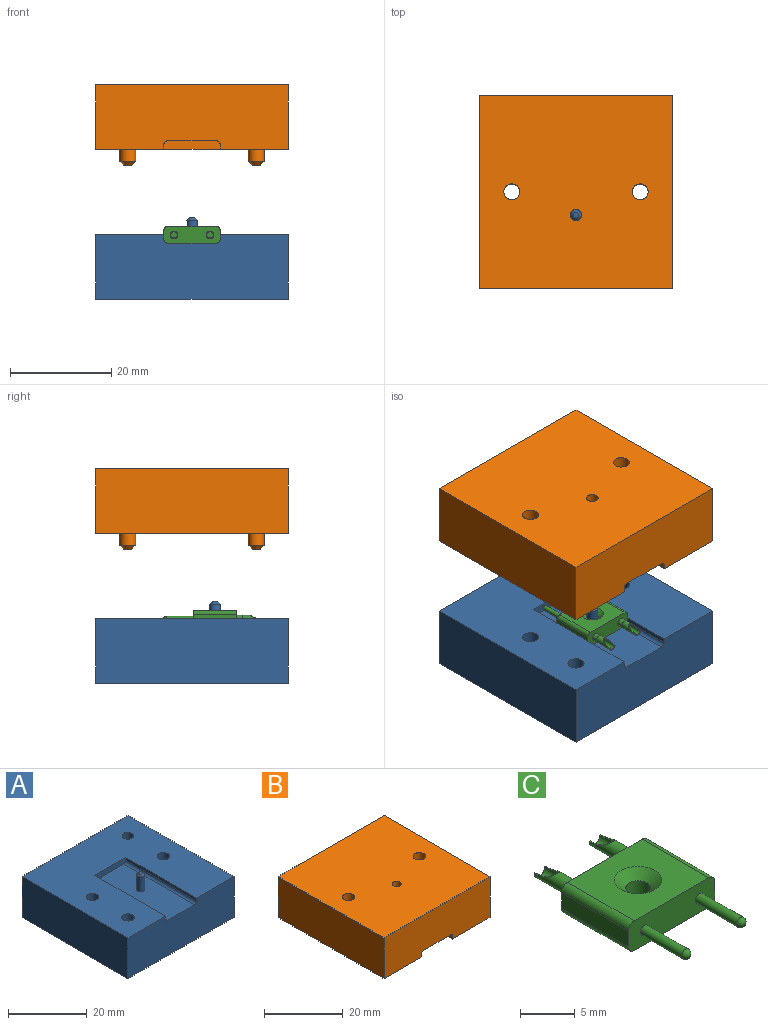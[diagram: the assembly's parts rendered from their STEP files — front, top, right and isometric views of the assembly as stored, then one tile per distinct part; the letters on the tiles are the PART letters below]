
ASSEMBLY  parts=3 mates=3
PART A: 21 faces, bbox 38.1x38.1x16.1 mm
  f0: plane 38.1x38.1mm, normal (0,0,1), area 1137.2mm2, adj f1,f2,f3,f4,f6,f7,f8,f13
  f1: plane 38.1x12.7mm, normal (-1,0,0), area 483.9mm2, adj f0,f2,f4,f5
  f2: plane 38.1x12.7mm, normal (0,-1,0), area 465.7mm2, adj f0,f1,f3,f5,f6,f7,f9,f19
  f3: plane 38.1x12.7mm, normal (1,0,0), area 483.9mm2, adj f0,f2,f4,f5
  f4: plane 38.1x12.7mm, normal (0,1,0), area 483.9mm2, adj f0,f1,f3,f5
  f5: plane 38.1x38.1mm, normal (0,0,-1), area 1435.8mm2, adj f1,f2,f3,f4,f13,f14
  f6: plane 25.4x0.89mm, normal (1,0,0), area 22.6mm2, adj f0,f2,f8,f20
  f7: plane 25.4x0.89mm, normal (-1,0,0), area 22.6mm2, adj f0,f2,f8,f19
  f8: plane 11.18x1.65mm, normal (0,-1,0), area 18.2mm2, adj f0,f6,f7,f9,f19,f20
  f9: plane 25.4x9.65mm, normal (0,0,1), area 241.5mm2, adj f2,f8,f10,f19,f20
  f10: cylinder r=1.08mm len=4.57mm, axis (0,0,-1), area 31mm2, adj f9,f12
  f11: plane 1.14x1.14mm, normal (0,0,1), area 1mm2, adj f12
  f12: cone r=0.57mm half-angle=45deg, axis (0,0,-1), area 3.7mm2, adj f10,f11
  f13: cylinder r=1.59mm len=12.7mm, axis (0,0,1), area 126.7mm2, adj f0,f5
  f14: cylinder r=1.59mm len=12.7mm, axis (0,0,1), area 126.7mm2, adj f0,f5
  f15: cylinder r=1.47mm len=6.35mm, axis (0,0,1), area 58.7mm2, adj f0,f16
  f16: plane 2.95x2.95mm, normal (0,0,1), area 6.8mm2, adj f15
  f17: cylinder r=1.59mm len=6.35mm, axis (0,0,1), area 63.3mm2, adj f0,f18
  f18: plane 3.18x3.18mm, normal (0,0,1), area 7.9mm2, adj f17
  f19: cylinder r=0.76mm len=25.4mm, axis (0,1,0), area 30.4mm2, adj f2,f7,f8,f9
  f20: cylinder r=0.76mm len=25.4mm, axis (0,-1,0), area 30.4mm2, adj f2,f6,f8,f9
PART B: 21 faces, bbox 38.1x38.1x15.9 mm
  f0: plane 38.1x38.1mm, normal (0,0,-1), area 1136.6mm2, adj f1,f2,f3,f4,f6,f7,f8,f13
  f1: plane 38.1x12.7mm, normal (-1,0,0), area 483.9mm2, adj f0,f2,f4,f5
  f2: plane 38.1x12.7mm, normal (0,-1,0), area 465.7mm2, adj f0,f1,f3,f5,f6,f8,f9,f11
  f3: plane 38.1x12.7mm, normal (1,0,0), area 483.9mm2, adj f0,f2,f4,f5
  f4: plane 38.1x12.7mm, normal (0,1,0), area 483.9mm2, adj f0,f1,f3,f5
  f5: plane 38.1x38.1mm, normal (0,0,1), area 1431.7mm2, adj f1,f2,f3,f4,f10,f13,f14
  f6: plane 25.4x0.89mm, normal (1,0,0), area 22.6mm2, adj f0,f2,f7,f11
  f7: plane 11.18x1.65mm, normal (0,-1,0), area 18.2mm2, adj f0,f6,f8,f9,f11,f12
  f8: plane 25.4x0.89mm, normal (-1,0,0), area 22.6mm2, adj f0,f2,f7,f12
  f9: plane 25.4x9.65mm, normal (0,0,-1), area 241.1mm2, adj f2,f7,f10,f11,f12
  f10: cylinder r=1.14mm len=11.05mm, axis (0,0,-1), area 79.4mm2, adj f5,f9
  f11: cylinder r=0.76mm len=25.4mm, axis (0,1,0), area 30.4mm2, adj f2,f6,f7,f9
  f12: cylinder r=0.76mm len=25.4mm, axis (0,-1,0), area 30.4mm2, adj f2,f7,f8,f9
  f13: cylinder r=1.59mm len=12.7mm, axis (0,0,-1), area 126.7mm2, adj f0,f5
  f14: cylinder r=1.59mm len=12.7mm, axis (0,0,-1), area 126.7mm2, adj f0,f5
  f15: cylinder r=1.56mm len=3.12mm, axis (0,0,1), area 23.7mm2, adj f0,f20
  f16: plane 1.6x1.6mm, normal (0,0,-1), area 2mm2, adj f20
  f17: cylinder r=1.56mm len=3.12mm, axis (0,0,1), area 23.7mm2, adj f0,f19
  f18: plane 1.6x1.6mm, normal (0,0,-1), area 2mm2, adj f19
  f19: cone r=0.8mm half-angle=45deg, axis (0,0,1), area 8mm2, adj f17,f18
  f20: cone r=0.8mm half-angle=45deg, axis (0,0,1), area 8mm2, adj f15,f16
PART C: 26 faces, bbox 11.2x19.3x3.3 mm
  f0: cylinder r=1.14mm len=2.42mm, axis (0,0,1), area 17.4mm2, adj f4,f21
  f1: plane 1.52x0.76mm, normal (0,1,0), area 0.3mm2, adj f13,f15,f20
  f2: plane 1.52x0.76mm, normal (0,1,0), area 0.3mm2, adj f14,f17,f19
  f3: plane 8.64x1.78mm, normal (-1,0,0), area 15.4mm2, adj f7,f8,f22,f25
  f4: plane 9.65x8.64mm, normal (0,0,-1), area 79.3mm2, adj f0,f7,f8,f22,f23
  f5: plane 8.64x1.78mm, normal (1,0,0), area 15.4mm2, adj f7,f8,f23,f24
  f6: plane 9.65x8.64mm, normal (0,0,1), area 68.7mm2, adj f7,f8,f21,f24,f25
  f7: plane 11.18x3.3mm, normal (0,1,0), area 32.8mm2, adj f3,f4,f5,f6,f13,f14,f22,f23
  f8: plane 11.18x3.3mm, normal (0,-1,0), area 34.8mm2, adj f3,f4,f5,f6,f9,f10,f22,f23
  f9: cylinder r=0.51mm len=5.33mm, axis (0,1,0), area 17mm2, adj f8,f12
  f10: cylinder r=0.51mm len=5.33mm, axis (0,1,0), area 17mm2, adj f8,f11
  f11: sphere r=0.51mm, area 1.6mm2, adj f10
  f12: sphere r=0.51mm, area 1.6mm2, adj f9
  f13: cylinder r=0.76mm len=4.83mm, axis (0,-1,0), area 18.8mm2, adj f1,f7,f20
  f14: cylinder r=0.76mm len=4.83mm, axis (0,-1,0), area 18.8mm2, adj f2,f7,f19
  f15: cylinder r=0.64mm len=3.81mm, axis (0,1,0), area 11.9mm2, adj f1,f16,f20
  f16: plane 1.27x1.27mm, normal (0,1,0), area 1.3mm2, adj f15
  f17: cylinder r=0.64mm len=3.81mm, axis (0,1,0), area 11.9mm2, adj f2,f18,f19
  f18: plane 1.27x1.27mm, normal (0,1,0), area 1.3mm2, adj f17
  f19: extruded ~2.29x1.52mm, area 0.8mm2, adj f2,f14,f17
  f20: extruded ~2.29x1.52mm, area 0.8mm2, adj f1,f13,f15
  f21: cone r=2.16mm half-angle=49deg, axis (0,0,1), area 14mm2, adj f0,f6
  f22: cylinder r=0.76mm len=8.64mm, axis (0,1,0), area 10.3mm2, adj f3,f4,f7,f8
  f23: cylinder r=0.76mm len=8.64mm, axis (0,-1,0), area 10.3mm2, adj f4,f5,f7,f8
  f24: cylinder r=0.76mm len=8.64mm, axis (0,1,0), area 10.3mm2, adj f5,f6,f7,f8
  f25: cylinder r=0.76mm len=8.64mm, axis (0,-1,0), area 10.3mm2, adj f3,f6,f7,f8
PLACE A t=(-7.87,2.78,9.25)mm
PLACE B t=(-7.87,2.78,38.92)mm
PLACE C rot(axis=(0,0,1),180deg) t=(16.77,21.57,20.3)mm
MATE cylindrical B.f15 <-> A.f17  axis (0,0,1) through (-1.52,9.13,36.51)mm
MATE cylindrical A.f15 <-> B.f17  axis (0,0,1) through (23.88,34.53,21.95)mm
MATE cylindrical C.f0 <-> A.f10  axis (0,0,-1) through (11.18,17.26,20.3)mm
